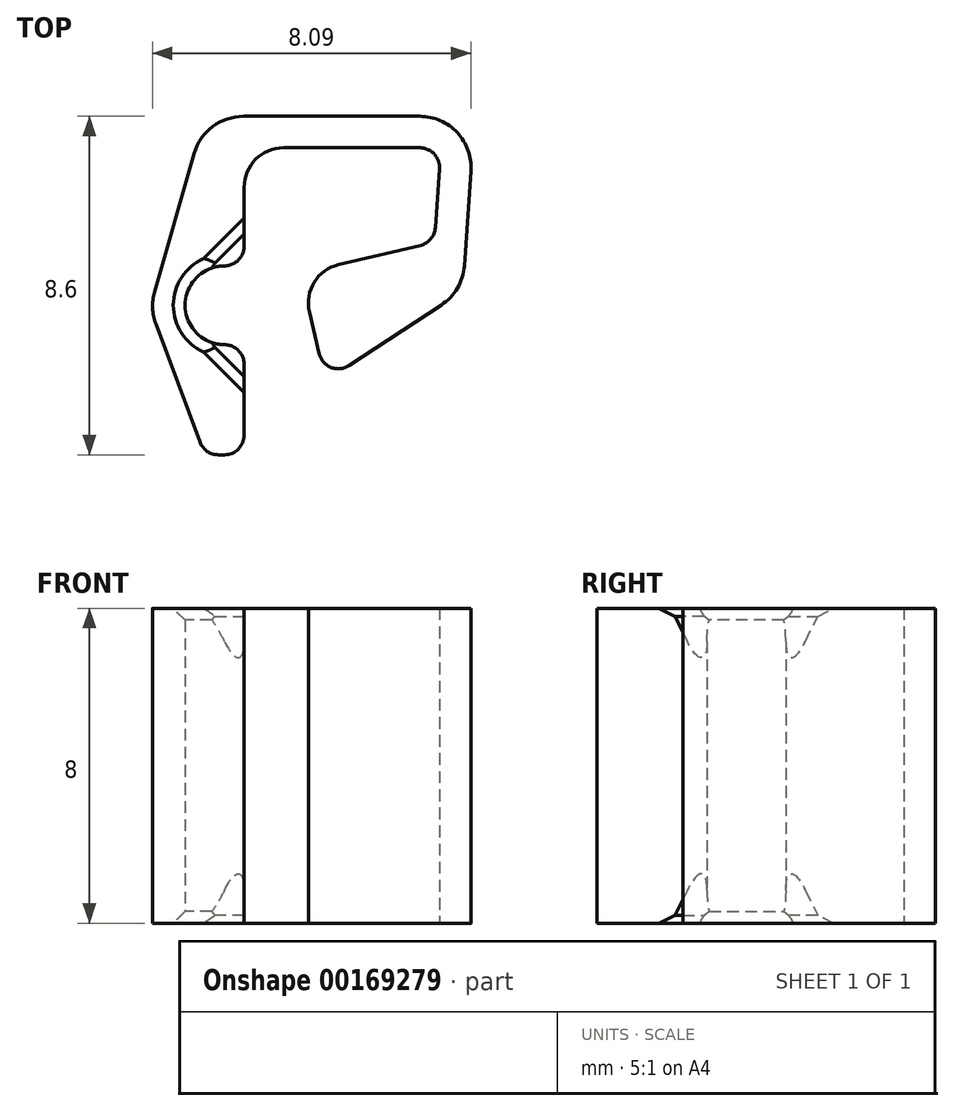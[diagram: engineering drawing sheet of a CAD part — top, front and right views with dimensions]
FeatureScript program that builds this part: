
annotation { "Feature Type Name" : "Feature", "Feature Type Description" : "" }
export const myFeature = defineFeature(function(context is Context, id is Id, definition is map)
    precondition{}
    {
        {
            var Q0;
            Q0=qCreatedBy(makeId("Top.planeOp"),FACE);
            var sketch = newSketch(context, id + "F0", { "sketchPlane" : qUnion([Q0])});
            skLineSegment(sketch, "E0", {"start": v(0, 0) * mm, "end": v(-0.17, -2.4) * mm});
            skLineSegment(sketch, "E1", {"start": v(-0.17, -2.4) * mm, "end": v(-3.57, -3.2) * mm});
            skLineSegment(sketch, "E2", {"start": v(-3.57, -3.2) * mm, "end": v(-2.93, -5.92) * mm});
            skLineSegment(sketch, "E3", {"start": v(-2.93, -5.92) * mm, "end": v(0.55, -3.64) * mm});
            skLineSegment(sketch, "E4", {"start": v(0.55, -3.64) * mm, "end": v(0.86, 0.8) * mm});
            skLineSegment(sketch, "E5", {"start": v(0.86, 0.8) * mm, "end": v(-6, 0.8) * mm});
            skLineSegment(sketch, "E6", {"start": v(-5.5, -5) * mm, "end": v(-5, -5) * mm});
            skLineSegment(sketch, "E7", {"start": v(-5, -5) * mm, "end": v(-5, -7.8) * mm});
            skLineSegment(sketch, "E8", {"start": v(-7.4, -4.08) * mm, "end": v(-6, -7.8) * mm});
            skLineSegment(sketch, "E9", {"start": v(-6, -7.8) * mm, "end": v(-5, -7.8) * mm});
            skLineSegment(sketch, "E10", {"start": v(-5, -3) * mm, "end": v(-5.5, -3) * mm});
            skLineSegment(sketch, "E11", {"start": v(0, 0) * mm, "end": v(-5, 0) * mm});
            skLineSegment(sketch, "E12", {"start": v(-5, 0) * mm, "end": v(-5, -3) * mm});
            skArc(sketch, "E13", {"start": v(-5.5, -3) * mm, "mid": v(-6.5, -4) * mm, "end": v(-5.5, -5) * mm});
            skLineSegment(sketch, "E14", {"start": v(-7.4, -4.08) * mm, "end": v(-6, 0.8) * mm});
            skLineSegment(sketch, "E15", {"start": v(-6, -7.8) * mm, "end": v(-6, 0.8) * mm, "construction": true});
            skLineSegment(sketch, "E16", {"start": v(-5.5, -4) * mm, "end": v(-6.46, -3.73) * mm, "construction": true});
            skLineSegment(sketch, "E17", {"start": v(-6.46, -3.73) * mm, "end": v(-7.23, -3.5) * mm, "construction": true});
            skLineSegment(sketch, "E18", {"start": v(0, 0) * mm, "end": v(0, 0.8) * mm, "construction": true});
            skLineSegment(sketch, "E19", {"start": v(0.8, -0.06) * mm, "end": v(0, 0) * mm, "construction": true});
            skLineSegment(sketch, "E20", {"start": v(-5.5, -4) * mm, "end": v(-6.44, -4.35) * mm, "construction": true});
            skLineSegment(sketch, "E21", {"start": v(-6.44, -4.35) * mm, "end": v(-7.19, -4.63) * mm, "construction": true});
            skSolve(sketch);
        }
        {
            var Q0;
            Q0=qSketchRegion(id+"F0",true);
            extrude(context, id + "F1", {"entities" : qUnion([Q0]), "depth" : 4 * mm});
        }
        {
            var Q0;
            Q0=makeQuery(id+"F1.opExtrude","CAP_FACE",FACE,{"disambiguationData":[OSD([sQuery(id+"F0.wireOp",EDGE,"E0"),sQuery(id+"F0.wireOp",EDGE,"E1"),sQuery(id+"F0.wireOp",EDGE,"E2"),sQuery(id+"F0.wireOp",EDGE,"E3"),sQuery(id+"F0.wireOp",EDGE,"E4"),sQuery(id+"F0.wireOp",EDGE,"E5"),sQuery(id+"F0.wireOp",EDGE,"3qQk4eZ2-qFBK-7vCE-47k8-9gwiF50xY8QG"),sQuery(id+"F0.wireOp",EDGE,"FwfflrWr-MbD4-lGZ7-AJjG-6BkzjliF19me"),sQuery(id+"F0.wireOp",EDGE,"E6"),sQuery(id+"F0.wireOp",EDGE,"E7"),sQuery(id+"F0.wireOp",EDGE,"dEJFUDGW-VdPt-nXIw-TINV-OlQtnsbTHH9Y"),sQuery(id+"F0.wireOp",EDGE,"E8"),sQuery(id+"F0.wireOp",EDGE,"E9")])],"isStart":false});
            var sketch = newSketch(context, id + "F2", { "sketchPlane" : qUnion([Q0])});
            skLineSegment(sketch, "E22", {"start": v(-6.2, -4.7) * mm, "end": v(-5, -5.91) * mm});
            skLineSegment(sketch, "E23", {"start": v(-5, -5.91) * mm, "end": v(-5, -5) * mm});
            skLineSegment(sketch, "E24", {"start": v(-5, -5) * mm, "end": v(-6.2, -4.7) * mm});
            skLineSegment(sketch, "E25", {"start": v(-6.2, -3.3) * mm, "end": v(-5, -2.09) * mm});
            skLineSegment(sketch, "E26", {"start": v(-5, -2.09) * mm, "end": v(-5, -3) * mm});
            skLineSegment(sketch, "E27", {"start": v(-5, -3) * mm, "end": v(-6.2, -3.3) * mm});
            skSolve(sketch);
        }
        {
            var Q0;
            Q0=qSketchRegion(id+"F2",true);
            extrude(context, id + "F3", {"entities" : qUnion([Q0]), "operationType" : NewBodyOperationType.REMOVE, "oppositeDirection" : true, "depth" : 2 * mm});
        }
        {
            var Q0;
            Q0=makeQuery(id+"F3.boolean.opBoolean","COPY",EDGE,{"derivedFrom":makeQuery(id+"F3.opExtrude","CAP_EDGE",EDGE,{"disambiguationData":[OSD([sQuery(id+"F2.wireOp",EDGE,"E22")])],"isStart":false})});
            chamfer(context, id + "F4", {"entities" : qUnion([Q0]), "chamferType" : ChamferType.TWO_OFFSETS, "width1" : .7 * mm, "oppositeDirection" : false, "width2" : 2 * mm, "tangentPropagation" : true});
        }
        {
            var Q0;
            Q0=makeQuery(id+"F3.boolean.opBoolean","COPY",EDGE,{"derivedFrom":makeQuery(id+"F3.opExtrude","CAP_EDGE",EDGE,{"disambiguationData":[OSD([sQuery(id+"F2.wireOp",EDGE,"E25")])],"isStart":false})});
            chamfer(context, id + "F5", {"entities" : qUnion([Q0]), "chamferType" : ChamferType.TWO_OFFSETS, "width1" : 2 * mm, "oppositeDirection" : false, "width2" : .7 * mm, "tangentPropagation" : true});
        }
        {
            var Q0;
            Q0=makeQuery(id+"F1.opExtrude","SWEPT_EDGE",EDGE,{"disambiguationData":[OSD([sQuery(id+"F0.wireOp",EDGE,"E0"),sQuery(id+"F0.wireOp",EDGE,"3qQk4eZ2-qFBK-7vCE-47k8-9gwiF50xY8QG")])]});
            var Q1;
            Q1=makeQuery(id+"F1.opExtrude","SWEPT_EDGE",EDGE,{"disambiguationData":[OSD([sQuery(id+"F0.wireOp",EDGE,"E0"),sQuery(id+"F0.wireOp",EDGE,"E1")])]});
            var Q2;
            Q2=makeQuery(id+"F1.opExtrude","SWEPT_EDGE",EDGE,{"disambiguationData":[OSD([sQuery(id+"F0.wireOp",EDGE,"E2"),sQuery(id+"F0.wireOp",EDGE,"E3")])]});
            var Q3;
            Q3=makeQuery(id+"F1.opExtrude","SWEPT_EDGE",EDGE,{"disambiguationData":[OSD([sQuery(id+"F0.wireOp",EDGE,"E7"),sQuery(id+"F0.wireOp",EDGE,"E9")])]});
            var Q4;
            Q4=makeQuery(id+"F1.opExtrude","SWEPT_EDGE",EDGE,{"disambiguationData":[OSD([sQuery(id+"F0.wireOp",EDGE,"E6"),sQuery(id+"F0.wireOp",EDGE,"E7")])]});
            var Q5;
            Q5=makeQuery(id+"F1.opExtrude","SWEPT_EDGE",EDGE,{"disambiguationData":[OSD([sQuery(id+"F0.wireOp",EDGE,"E10"),sQuery(id+"F0.wireOp",EDGE,"E12")])]});
            var Q6;
            Q6=makeQuery(id+"F1.opExtrude","SWEPT_EDGE",EDGE,{"disambiguationData":[OSD([sQuery(id+"F0.wireOp",EDGE,"E8"),sQuery(id+"F0.wireOp",EDGE,"E9")])]});
            fillet(context, id + "F6", {"entities" : qUnion([Q0, Q1, Q2, Q3, Q4, Q5, Q6]), "radius" : .5 * mm, "tangentPropagation" : true, "allowEdgeOverflow" : false});
        }
        {
            var Q0;
            Q0=makeQuery(id+"F1.opExtrude","SWEPT_EDGE",EDGE,{"disambiguationData":[OSD([sQuery(id+"F0.wireOp",EDGE,"E11"),sQuery(id+"F0.wireOp",EDGE,"E12")])]});
            var Q1;
            Q1=makeQuery(id+"F1.opExtrude","SWEPT_EDGE",EDGE,{"disambiguationData":[OSD([sQuery(id+"F0.wireOp",EDGE,"E1"),sQuery(id+"F0.wireOp",EDGE,"E2")])]});
            fillet(context, id + "F7", {"entities" : qUnion([Q0, Q1]), "radius" : 1 * mm, "tangentPropagation" : true, "allowEdgeOverflow" : false});
        }
        {
            var Q0;
            Q0=makeQuery(id+"F1.opExtrude","SWEPT_EDGE",EDGE,{"disambiguationData":[OSD([sQuery(id+"F0.wireOp",EDGE,"E4"),sQuery(id+"F0.wireOp",EDGE,"E5")])]});
            var Q1;
            Q1=makeQuery(id+"F1.opExtrude","SWEPT_EDGE",EDGE,{"disambiguationData":[OSD([sQuery(id+"F0.wireOp",EDGE,"E3"),sQuery(id+"F0.wireOp",EDGE,"E4")])]});
            var Q2;
            Q2=makeQuery(id+"F1.opExtrude","SWEPT_EDGE",EDGE,{"disambiguationData":[OSD([sQuery(id+"F0.wireOp",EDGE,"E8"),sQuery(id+"F0.wireOp",EDGE,"E9")])]});
            var Q3;
            Q3=makeQuery(id+"F1.opExtrude","SWEPT_EDGE",EDGE,{"disambiguationData":[OSD([sQuery(id+"F0.wireOp",EDGE,"E8"),sQuery(id+"F0.wireOp",EDGE,"E14")])]});
            var Q4;
            Q4=makeQuery(id+"F1.opExtrude","SWEPT_EDGE",EDGE,{"disambiguationData":[OSD([sQuery(id+"F0.wireOp",EDGE,"E5"),sQuery(id+"F0.wireOp",EDGE,"E14")])]});
            fillet(context, id + "F8", {"entities" : qUnion([Q0, Q1, Q2, Q3, Q4]), "radius" : 1.3 * mm, "tangentPropagation" : true, "allowEdgeOverflow" : false});
        }
        {
            var Q0;
            Q0=makeQuery(id+"F1.opExtrude","SWEPT_BODY",BODY,{"disambiguationData":[OSD([sQuery(id+"F0.wireOp",EDGE,"E0"),sQuery(id+"F0.wireOp",EDGE,"E1"),sQuery(id+"F0.wireOp",EDGE,"E2"),sQuery(id+"F0.wireOp",EDGE,"E3"),sQuery(id+"F0.wireOp",EDGE,"E4"),sQuery(id+"F0.wireOp",EDGE,"E5"),sQuery(id+"F0.wireOp",EDGE,"3qQk4eZ2-qFBK-7vCE-47k8-9gwiF50xY8QG"),sQuery(id+"F0.wireOp",EDGE,"FwfflrWr-MbD4-lGZ7-AJjG-6BkzjliF19me"),sQuery(id+"F0.wireOp",EDGE,"E6"),sQuery(id+"F0.wireOp",EDGE,"E7"),sQuery(id+"F0.wireOp",EDGE,"dEJFUDGW-VdPt-nXIw-TINV-OlQtnsbTHH9Y"),sQuery(id+"F0.wireOp",EDGE,"E8"),sQuery(id+"F0.wireOp",EDGE,"E9")])]});
            var Q1;
            Q1=makeQuery(id+"F1.opExtrude","CAP_FACE",FACE,{"disambiguationData":[OSD([sQuery(id+"F0.wireOp",EDGE,"E0"),sQuery(id+"F0.wireOp",EDGE,"E1"),sQuery(id+"F0.wireOp",EDGE,"E2"),sQuery(id+"F0.wireOp",EDGE,"E3"),sQuery(id+"F0.wireOp",EDGE,"E4"),sQuery(id+"F0.wireOp",EDGE,"E5"),sQuery(id+"F0.wireOp",EDGE,"3qQk4eZ2-qFBK-7vCE-47k8-9gwiF50xY8QG"),sQuery(id+"F0.wireOp",EDGE,"FwfflrWr-MbD4-lGZ7-AJjG-6BkzjliF19me"),sQuery(id+"F0.wireOp",EDGE,"E6"),sQuery(id+"F0.wireOp",EDGE,"E7"),sQuery(id+"F0.wireOp",EDGE,"dEJFUDGW-VdPt-nXIw-TINV-OlQtnsbTHH9Y"),sQuery(id+"F0.wireOp",EDGE,"E8"),sQuery(id+"F0.wireOp",EDGE,"E9")])],"isStart":true});
            mirror(context, id + "F9", {"operationType" : NewBodyOperationType.ADD, "entities" : qUnion([Q0]), "mirrorPlane" : qUnion([Q1])});
        }
        {
            var Q0;
            Q0=makeQuery(id+"F1.opExtrude","CAP_EDGE",EDGE,{"disambiguationData":[OSD([sQuery(id+"F0.wireOp",EDGE,"E13")])],"isStart":false});
            var Q1;
            Q1=makeQuery(id+"F5.opChamfer","BLEND_EDGE",EDGE,{"blendedFrom":[makeQuery(id+"F3.boolean.opBoolean","COPY",EDGE,{"derivedFrom":makeQuery(id+"F3.opExtrude","CAP_EDGE",EDGE,{"disambiguationData":[OSD([sQuery(id+"F2.wireOp",EDGE,"E25")])],"isStart":false})}),makeQuery(id+"F1.opExtrude","CAP_FACE",FACE,{"disambiguationData":[OSD([sQuery(id+"F0.wireOp",EDGE,"E0"),sQuery(id+"F0.wireOp",EDGE,"E1"),sQuery(id+"F0.wireOp",EDGE,"E2"),sQuery(id+"F0.wireOp",EDGE,"E3"),sQuery(id+"F0.wireOp",EDGE,"E4"),sQuery(id+"F0.wireOp",EDGE,"E5"),sQuery(id+"F0.wireOp",EDGE,"E6"),sQuery(id+"F0.wireOp",EDGE,"E7"),sQuery(id+"F0.wireOp",EDGE,"E8"),sQuery(id+"F0.wireOp",EDGE,"E9"),sQuery(id+"F0.wireOp",EDGE,"E10"),sQuery(id+"F0.wireOp",EDGE,"E11"),sQuery(id+"F0.wireOp",EDGE,"E12"),sQuery(id+"F0.wireOp",EDGE,"E13"),sQuery(id+"F0.wireOp",EDGE,"E14")])],"isStart":false})],"blendedInto":[makeQuery(id+"F1.opExtrude","CAP_FACE",FACE,{"disambiguationData":[OSD([sQuery(id+"F0.wireOp",EDGE,"E0"),sQuery(id+"F0.wireOp",EDGE,"E1"),sQuery(id+"F0.wireOp",EDGE,"E2"),sQuery(id+"F0.wireOp",EDGE,"E3"),sQuery(id+"F0.wireOp",EDGE,"E4"),sQuery(id+"F0.wireOp",EDGE,"E5"),sQuery(id+"F0.wireOp",EDGE,"E6"),sQuery(id+"F0.wireOp",EDGE,"E7"),sQuery(id+"F0.wireOp",EDGE,"E8"),sQuery(id+"F0.wireOp",EDGE,"E9"),sQuery(id+"F0.wireOp",EDGE,"E10"),sQuery(id+"F0.wireOp",EDGE,"E11"),sQuery(id+"F0.wireOp",EDGE,"E12"),sQuery(id+"F0.wireOp",EDGE,"E13"),sQuery(id+"F0.wireOp",EDGE,"E14")])],"isStart":false})]});
            var Q2;
            Q2=makeQuery(id+"F4.opChamfer","BLEND_EDGE",EDGE,{"blendedFrom":[makeQuery(id+"F3.boolean.opBoolean","COPY",EDGE,{"derivedFrom":makeQuery(id+"F3.opExtrude","CAP_EDGE",EDGE,{"disambiguationData":[OSD([sQuery(id+"F2.wireOp",EDGE,"E22")])],"isStart":false})}),makeQuery(id+"F1.opExtrude","CAP_FACE",FACE,{"disambiguationData":[OSD([sQuery(id+"F0.wireOp",EDGE,"E0"),sQuery(id+"F0.wireOp",EDGE,"E1"),sQuery(id+"F0.wireOp",EDGE,"E2"),sQuery(id+"F0.wireOp",EDGE,"E3"),sQuery(id+"F0.wireOp",EDGE,"E4"),sQuery(id+"F0.wireOp",EDGE,"E5"),sQuery(id+"F0.wireOp",EDGE,"E6"),sQuery(id+"F0.wireOp",EDGE,"E7"),sQuery(id+"F0.wireOp",EDGE,"E8"),sQuery(id+"F0.wireOp",EDGE,"E9"),sQuery(id+"F0.wireOp",EDGE,"E10"),sQuery(id+"F0.wireOp",EDGE,"E11"),sQuery(id+"F0.wireOp",EDGE,"E12"),sQuery(id+"F0.wireOp",EDGE,"E13"),sQuery(id+"F0.wireOp",EDGE,"E14")])],"isStart":false})],"blendedInto":[makeQuery(id+"F1.opExtrude","CAP_FACE",FACE,{"disambiguationData":[OSD([sQuery(id+"F0.wireOp",EDGE,"E0"),sQuery(id+"F0.wireOp",EDGE,"E1"),sQuery(id+"F0.wireOp",EDGE,"E2"),sQuery(id+"F0.wireOp",EDGE,"E3"),sQuery(id+"F0.wireOp",EDGE,"E4"),sQuery(id+"F0.wireOp",EDGE,"E5"),sQuery(id+"F0.wireOp",EDGE,"E6"),sQuery(id+"F0.wireOp",EDGE,"E7"),sQuery(id+"F0.wireOp",EDGE,"E8"),sQuery(id+"F0.wireOp",EDGE,"E9"),sQuery(id+"F0.wireOp",EDGE,"E10"),sQuery(id+"F0.wireOp",EDGE,"E11"),sQuery(id+"F0.wireOp",EDGE,"E12"),sQuery(id+"F0.wireOp",EDGE,"E13"),sQuery(id+"F0.wireOp",EDGE,"E14")])],"isStart":false})]});
            var Q3;
            Q3=makeQuery(id+"F9.opPattern","COPY",EDGE,{"derivedFrom":makeQuery(id+"F1.opExtrude","CAP_EDGE",EDGE,{"disambiguationData":[OSD([sQuery(id+"F0.wireOp",EDGE,"E13")])],"isStart":false}),"instanceName":"1"});
            var Q4;
            Q4=makeQuery(id+"F9.opPattern","COPY",EDGE,{"derivedFrom":makeQuery(id+"F5.opChamfer","BLEND_EDGE",EDGE,{"blendedFrom":[makeQuery(id+"F3.boolean.opBoolean","COPY",EDGE,{"derivedFrom":makeQuery(id+"F3.opExtrude","CAP_EDGE",EDGE,{"disambiguationData":[OSD([sQuery(id+"F2.wireOp",EDGE,"E25")])],"isStart":false})}),makeQuery(id+"F1.opExtrude","CAP_FACE",FACE,{"disambiguationData":[OSD([sQuery(id+"F0.wireOp",EDGE,"E0"),sQuery(id+"F0.wireOp",EDGE,"E1"),sQuery(id+"F0.wireOp",EDGE,"E2"),sQuery(id+"F0.wireOp",EDGE,"E3"),sQuery(id+"F0.wireOp",EDGE,"E4"),sQuery(id+"F0.wireOp",EDGE,"E5"),sQuery(id+"F0.wireOp",EDGE,"E6"),sQuery(id+"F0.wireOp",EDGE,"E7"),sQuery(id+"F0.wireOp",EDGE,"E8"),sQuery(id+"F0.wireOp",EDGE,"E9"),sQuery(id+"F0.wireOp",EDGE,"E10"),sQuery(id+"F0.wireOp",EDGE,"E11"),sQuery(id+"F0.wireOp",EDGE,"E12"),sQuery(id+"F0.wireOp",EDGE,"E13"),sQuery(id+"F0.wireOp",EDGE,"E14")])],"isStart":false})],"blendedInto":[makeQuery(id+"F1.opExtrude","CAP_FACE",FACE,{"disambiguationData":[OSD([sQuery(id+"F0.wireOp",EDGE,"E0"),sQuery(id+"F0.wireOp",EDGE,"E1"),sQuery(id+"F0.wireOp",EDGE,"E2"),sQuery(id+"F0.wireOp",EDGE,"E3"),sQuery(id+"F0.wireOp",EDGE,"E4"),sQuery(id+"F0.wireOp",EDGE,"E5"),sQuery(id+"F0.wireOp",EDGE,"E6"),sQuery(id+"F0.wireOp",EDGE,"E7"),sQuery(id+"F0.wireOp",EDGE,"E8"),sQuery(id+"F0.wireOp",EDGE,"E9"),sQuery(id+"F0.wireOp",EDGE,"E10"),sQuery(id+"F0.wireOp",EDGE,"E11"),sQuery(id+"F0.wireOp",EDGE,"E12"),sQuery(id+"F0.wireOp",EDGE,"E13"),sQuery(id+"F0.wireOp",EDGE,"E14")])],"isStart":false})]}),"instanceName":"1"});
            var Q5;
            Q5=makeQuery(id+"F9.opPattern","COPY",EDGE,{"derivedFrom":makeQuery(id+"F4.opChamfer","BLEND_EDGE",EDGE,{"blendedFrom":[makeQuery(id+"F3.boolean.opBoolean","COPY",EDGE,{"derivedFrom":makeQuery(id+"F3.opExtrude","CAP_EDGE",EDGE,{"disambiguationData":[OSD([sQuery(id+"F2.wireOp",EDGE,"E22")])],"isStart":false})}),makeQuery(id+"F1.opExtrude","CAP_FACE",FACE,{"disambiguationData":[OSD([sQuery(id+"F0.wireOp",EDGE,"E0"),sQuery(id+"F0.wireOp",EDGE,"E1"),sQuery(id+"F0.wireOp",EDGE,"E2"),sQuery(id+"F0.wireOp",EDGE,"E3"),sQuery(id+"F0.wireOp",EDGE,"E4"),sQuery(id+"F0.wireOp",EDGE,"E5"),sQuery(id+"F0.wireOp",EDGE,"E6"),sQuery(id+"F0.wireOp",EDGE,"E7"),sQuery(id+"F0.wireOp",EDGE,"E8"),sQuery(id+"F0.wireOp",EDGE,"E9"),sQuery(id+"F0.wireOp",EDGE,"E10"),sQuery(id+"F0.wireOp",EDGE,"E11"),sQuery(id+"F0.wireOp",EDGE,"E12"),sQuery(id+"F0.wireOp",EDGE,"E13"),sQuery(id+"F0.wireOp",EDGE,"E14")])],"isStart":false})],"blendedInto":[makeQuery(id+"F1.opExtrude","CAP_FACE",FACE,{"disambiguationData":[OSD([sQuery(id+"F0.wireOp",EDGE,"E0"),sQuery(id+"F0.wireOp",EDGE,"E1"),sQuery(id+"F0.wireOp",EDGE,"E2"),sQuery(id+"F0.wireOp",EDGE,"E3"),sQuery(id+"F0.wireOp",EDGE,"E4"),sQuery(id+"F0.wireOp",EDGE,"E5"),sQuery(id+"F0.wireOp",EDGE,"E6"),sQuery(id+"F0.wireOp",EDGE,"E7"),sQuery(id+"F0.wireOp",EDGE,"E8"),sQuery(id+"F0.wireOp",EDGE,"E9"),sQuery(id+"F0.wireOp",EDGE,"E10"),sQuery(id+"F0.wireOp",EDGE,"E11"),sQuery(id+"F0.wireOp",EDGE,"E12"),sQuery(id+"F0.wireOp",EDGE,"E13"),sQuery(id+"F0.wireOp",EDGE,"E14")])],"isStart":false})]}),"instanceName":"1"});
            chamfer(context, id + "F10", {"entities" : qUnion([Q0, Q1, Q2, Q3, Q4, Q5]), "chamferType" : ChamferType.OFFSET_ANGLE, "width" : .3 * mm, "oppositeDirection" : false, "angle" : 45 * degree, "tangentPropagation" : true});
        }
    });
